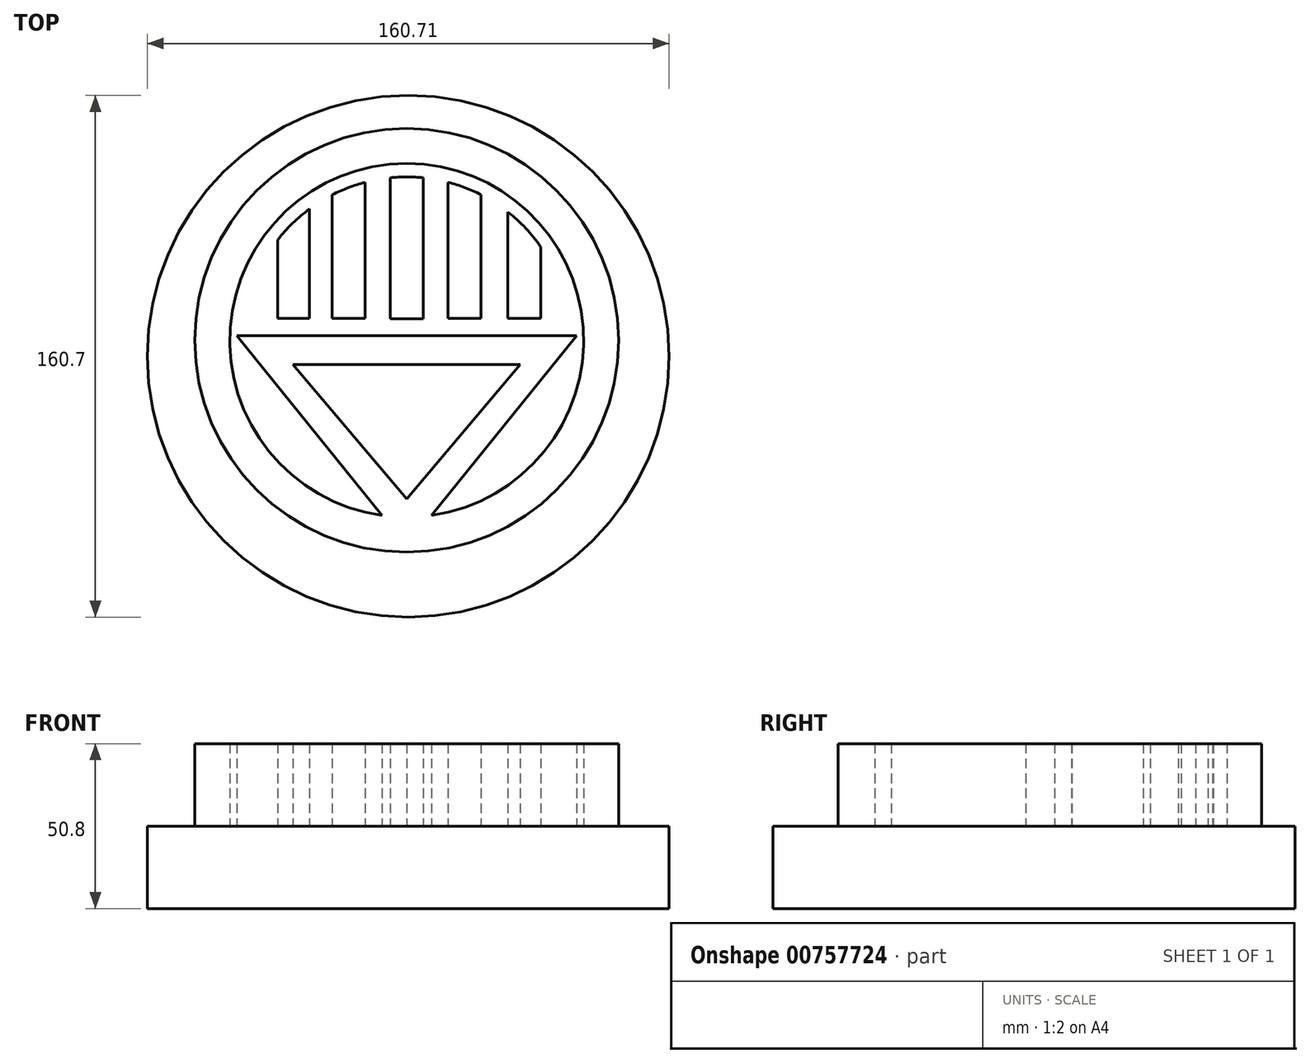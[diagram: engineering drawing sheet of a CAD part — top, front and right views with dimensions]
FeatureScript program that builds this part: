
annotation { "Feature Type Name" : "Feature", "Feature Type Description" : "" }
export const myFeature = defineFeature(function(context is Context, id is Id, definition is map)
    precondition{}
    {
        {
            var Q0;
            Q0=qCreatedBy(makeId("Top.planeOp"),FACE);
            var sketch = newSketch(context, id + "F0", { "sketchPlane" : qUnion([Q0])});
            skCircle(sketch, "E0", {"center": v(71.12, 76.08) * mm, "radius": 65.26 * mm});
            skArc(sketch, "E1", {"start": v(78.73, 22.13) * mm, "mid": v(71.12, 130.56) * mm, "end": v(63.51, 22.13) * mm});
            skLineSegment(sketch, "E2", {"start": v(78.73, 22.13) * mm, "end": v(123.42, 77.54) * mm});
            skLineSegment(sketch, "E3", {"start": v(123.42, 77.54) * mm, "end": v(71.12, 77.54) * mm});
            skLineSegment(sketch, "E4", {"start": v(106.12, 68.58) * mm, "end": v(71.12, 27.26) * mm});
            skLineSegment(sketch, "E5.MirrorCS", {"start": v(63.51, 22.13) * mm, "end": v(18.82, 77.54) * mm});
            skLineSegment(sketch, "E6.MirrorCS", {"start": v(36.12, 68.58) * mm, "end": v(71.12, 27.26) * mm});
            skLineSegment(sketch, "E7.MirrorCS", {"start": v(71.12, 68.58) * mm, "end": v(36.12, 68.58) * mm});
            skLineSegment(sketch, "E8", {"start": v(36.12, 68.58) * mm, "end": v(106.12, 68.58) * mm});
            skLineSegment(sketch, "E9", {"start": v(71.12, 27.26) * mm, "end": v(36.12, 68.58) * mm});
            skLineSegment(sketch, "E10", {"start": v(18.82, 77.54) * mm, "end": v(123.42, 77.54) * mm});
            skLineSegment(sketch, "E11", {"start": v(76.2, 82.7) * mm, "end": v(76.2, 126.17) * mm});
            skLineSegment(sketch, "E12", {"start": v(83.89, 82.84) * mm, "end": v(83.89, 124.78) * mm});
            skLineSegment(sketch, "E13", {"start": v(94.05, 82.84) * mm, "end": v(94.05, 120.9) * mm});
            skLineSegment(sketch, "E14", {"start": v(83.89, 82.84) * mm, "end": v(94.05, 82.84) * mm});
            skLineSegment(sketch, "E15", {"start": v(102.31, 82.84) * mm, "end": v(102.31, 115.6) * mm});
            skLineSegment(sketch, "E16", {"start": v(112.47, 82.84) * mm, "end": v(112.47, 104.8) * mm});
            skLineSegment(sketch, "E17", {"start": v(102.31, 82.84) * mm, "end": v(112.47, 82.84) * mm});
            skLineSegment(sketch, "E18.MirrorCS", {"start": v(66.04, 82.7) * mm, "end": v(66.04, 126.17) * mm});
            skLineSegment(sketch, "E19.MirrorCS", {"start": v(58.35, 82.84) * mm, "end": v(58.35, 124.78) * mm});
            skLineSegment(sketch, "E20.MirrorCS", {"start": v(58.35, 82.84) * mm, "end": v(48.2, 82.84) * mm});
            skLineSegment(sketch, "E21.MirrorCS", {"start": v(48.2, 82.84) * mm, "end": v(48.2, 120.9) * mm});
            skLineSegment(sketch, "E22", {"start": v(66.04, 82.7) * mm, "end": v(76.2, 82.7) * mm});
            skLineSegment(sketch, "E23", {"start": v(41.21, 82.84) * mm, "end": v(41.21, 116.58) * mm});
            skLineSegment(sketch, "E24", {"start": v(31.35, 82.84) * mm, "end": v(31.35, 106.96) * mm});
            skLineSegment(sketch, "E25", {"start": v(31.35, 82.84) * mm, "end": v(41.21, 82.84) * mm});
            skArc(sketch, "E26.trimOffspring", {"start": v(112.47, 104.8) * mm, "mid": v(107.8, 110.58) * mm, "end": v(102.31, 115.6) * mm});
            skArc(sketch, "E27.trimOffspring", {"start": v(41.21, 116.58) * mm, "mid": v(35.95, 112.1) * mm, "end": v(31.35, 106.96) * mm});
            skArc(sketch, "E28.trimOffspring", {"start": v(58.35, 124.78) * mm, "mid": v(53.17, 123.12) * mm, "end": v(48.2, 120.9) * mm});
            skArc(sketch, "E29.trimOffspring", {"start": v(76.2, 126.17) * mm, "mid": v(71.12, 126.43) * mm, "end": v(66.04, 126.17) * mm});
            skArc(sketch, "E30.trimOffspring", {"start": v(94.05, 120.9) * mm, "mid": v(89.07, 123.12) * mm, "end": v(83.89, 124.78) * mm});
            skSolve(sketch);
        }
        {
            var Q0;
            Q0=qCreatedBy(makeId("Top.planeOp"),FACE);
            var sketch = newSketch(context, id + "F1", { "sketchPlane" : qUnion([Q0])});
            skCircle(sketch, "E31", {"center": v(71.6, 71.17) * mm, "radius": 80.35 * mm});
            skSolve(sketch);
        }
        {
            var Q0;
            Q0 = qSketchRegion(id + "F1", true);
            extrude(context, id + "F2", {"entities" : qUnion([Q0]), "oppositeDirection" : true, "depth" : 25.4 * mm, "offsetDistance" : 25.4 * mm});
        }
        {
            var Q0;
            Q0=makeQuery(id+"F0.imprint","IMPRINT",FACE,{"disambiguationData":[TD([[makeQuery(id+"F0.imprint","IMPRINT",EDGE,{"derivedFrom":sQuery(id+"F0.wireOp",EDGE,"E0")}),1.0]])]});
            var Q1;
            Q1=makeQuery(id+"F0.imprint","IMPRINT",FACE,{"disambiguationData":[TD([[makeQuery(id+"F0.imprint","IMPRINT",EDGE,{"derivedFrom":sQuery(id+"F0.wireOp",EDGE,"E23")}),1.0]])]});
            var Q2;
            Q2=makeQuery(id+"F0.imprint","IMPRINT",FACE,{"disambiguationData":[TD([[makeQuery(id+"F0.imprint","IMPRINT",EDGE,{"derivedFrom":sQuery(id+"F0.wireOp",EDGE,"E19.MirrorCS")}),1.0]])]});
            var Q3;
            Q3=makeQuery(id+"F0.imprint","IMPRINT",FACE,{"disambiguationData":[TD([[makeQuery(id+"F0.imprint","IMPRINT",EDGE,{"derivedFrom":sQuery(id+"F0.wireOp",EDGE,"E11")}),1.0]])]});
            var Q4;
            Q4=makeQuery(id+"F0.imprint","IMPRINT",FACE,{"disambiguationData":[TD([[makeQuery(id+"F0.imprint","IMPRINT",EDGE,{"derivedFrom":sQuery(id+"F0.wireOp",EDGE,"E12")}),-1.0]])]});
            var Q5;
            Q5=makeQuery(id+"F0.imprint","IMPRINT",FACE,{"disambiguationData":[TD([[makeQuery(id+"F0.imprint","IMPRINT",EDGE,{"derivedFrom":sQuery(id+"F0.wireOp",EDGE,"E15")}),-1.0]])]});
            extrude(context, id + "F3", {"entities" : qUnion([Q0, Q1, Q2, Q3, Q4, Q5]), "operationType" : NewBodyOperationType.ADD, "depth" : 25.4 * mm, "offsetDistance" : 25.4 * mm});
        }
    });
